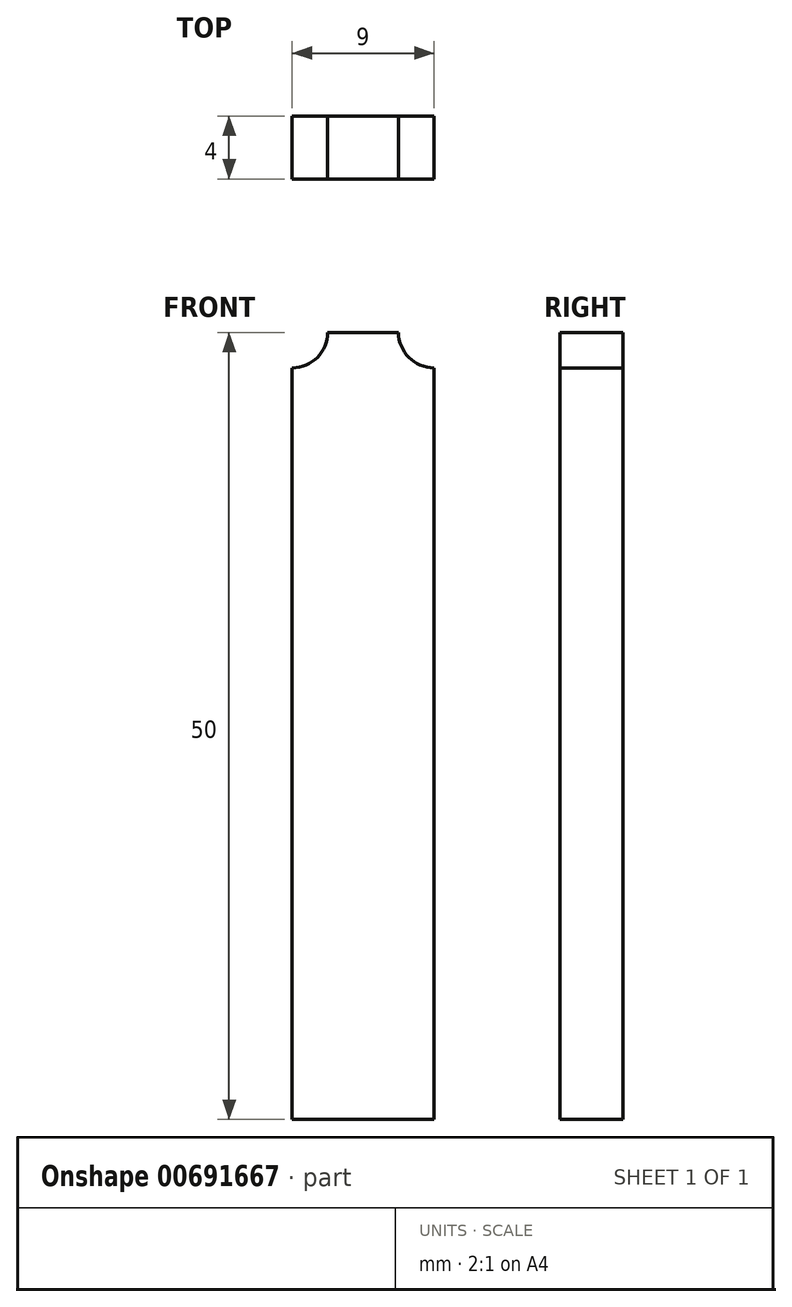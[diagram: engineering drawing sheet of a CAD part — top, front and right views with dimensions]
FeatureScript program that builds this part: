
annotation { "Feature Type Name" : "Feature", "Feature Type Description" : "" }
export const myFeature = defineFeature(function(context is Context, id is Id, definition is map)
    precondition{}
    {
        {
            var Q0;
            Q0=qCreatedBy(makeId("Front.planeOp"),FACE);
            var sketch = newSketch(context, id + "F0", { "sketchPlane" : qUnion([Q0])});
            skLineSegment(sketch, "E0.bottom", {"start": v(-4.5, 0) * mm, "end": v(4.5, 0) * mm});
            skLineSegment(sketch, "E0.top", {"start": v(-4.5, -50) * mm, "end": v(4.5, -50) * mm});
            skLineSegment(sketch, "E0.left", {"start": v(-4.5, 0) * mm, "end": v(-4.5, -50) * mm});
            skLineSegment(sketch, "E0.right", {"start": v(4.5, 0) * mm, "end": v(4.5, -50) * mm});
            skLineSegment(sketch, "E1.bottom", {"start": v(-2.25, 29.05) * mm, "end": v(2.25, 29.05) * mm});
            skLineSegment(sketch, "E1.top", {"start": v(-2.25, 0) * mm, "end": v(2.25, 0) * mm});
            skLineSegment(sketch, "E1.left", {"start": v(-2.25, 29.05) * mm, "end": v(-2.25, 0) * mm});
            skLineSegment(sketch, "E1.right", {"start": v(2.25, 29.05) * mm, "end": v(2.25, 0) * mm});
            skLineSegment(sketch, "E2", {"start": v(0, 22) * mm, "end": v(0, 13) * mm});
            skLineSegment(sketch, "E3.bottom", {"start": v(33.74, -3.72) * mm, "end": v(46.18, -3.72) * mm});
            skLineSegment(sketch, "E3.top", {"start": v(33.74, -42.5) * mm, "end": v(46.18, -42.5) * mm});
            skLineSegment(sketch, "E3.left", {"start": v(33.74, -3.72) * mm, "end": v(33.74, -42.5) * mm});
            skLineSegment(sketch, "E3.right", {"start": v(46.18, -3.72) * mm, "end": v(46.18, -42.5) * mm});
            skLineSegment(sketch, "E4", {"start": v(46.18, -8.55) * mm, "end": v(42.11, -6.2) * mm});
            skLineSegment(sketch, "E5", {"start": v(42.11, -6.2) * mm, "end": v(42.11, -13.68) * mm});
            skLineSegment(sketch, "E6", {"start": v(42.11, -13.68) * mm, "end": v(46.18, -11.33) * mm});
            skLineSegment(sketch, "E7.0.1.0", {"start": v(46.18, -20.55) * mm, "end": v(42.11, -18.2) * mm});
            skLineSegment(sketch, "E7.0.1.1", {"start": v(42.11, -18.2) * mm, "end": v(42.11, -25.68) * mm});
            skLineSegment(sketch, "E7.0.1.2", {"start": v(42.11, -25.68) * mm, "end": v(46.18, -23.33) * mm});
            skLineSegment(sketch, "E7.0.2.0", {"start": v(46.18, -32.55) * mm, "end": v(42.11, -30.2) * mm});
            skLineSegment(sketch, "E7.0.2.1", {"start": v(42.11, -30.2) * mm, "end": v(42.11, -37.68) * mm});
            skLineSegment(sketch, "E7.0.2.2", {"start": v(42.11, -37.68) * mm, "end": v(46.18, -35.33) * mm});
            skLineSegment(sketch, "E7.direction1", {"start": v(42.11, -13.68) * mm, "end": v(67.11, -13.68) * mm, "construction": true});
            skLineSegment(sketch, "E7.direction2", {"start": v(42.11, -13.68) * mm, "end": v(42.11, -25.68) * mm, "construction": true});
            skLineSegment(sketch, "E8.0", {"start": v(41.91, -14.03) * mm, "end": v(46.18, -11.57) * mm});
            skLineSegment(sketch, "E8.1", {"start": v(41.91, -5.86) * mm, "end": v(41.91, -14.03) * mm});
            skLineSegment(sketch, "E8.2", {"start": v(46.18, -8.32) * mm, "end": v(41.91, -5.86) * mm});
            skArc(sketch, "E9.0.startCap", {"start": v(-1, 22) * mm, "mid": v(0, 23) * mm, "end": v(1, 22) * mm});
            skArc(sketch, "E9.0.endCap", {"start": v(1, 13) * mm, "mid": v(0, 12) * mm, "end": v(-1, 13) * mm});
            skLineSegment(sketch, "E9.0.left", {"start": v(1, 22) * mm, "end": v(1, 13) * mm});
            skLineSegment(sketch, "E9.0.right", {"start": v(-1, 22) * mm, "end": v(-1, 13) * mm});
            skFitSpline(sketch, "E10", {"points": [v(0, 29.05) * mm, v(-1.01, 28.43) * mm, v(-1.8, 25.53) * mm, v(-2.25, 21.02) * mm], "startDerivative": vector(-5.04, -1.79) * mm, "endDerivative": vector(-0.93, -10.66) * mm});
            skFitSpline(sketch, "E11.MirrorCS", {"points": [v(0, 29.05) * mm, v(1.01, 28.43) * mm, v(1.8, 25.53) * mm, v(2.25, 21.02) * mm], "startDerivative": vector(5.04, -1.79) * mm, "endDerivative": vector(0.93, -10.66) * mm});
            skSolve(sketch);
        }
        {
            var Q0;
            {var subQ1=sQuery(id+"F0.wireOp",EDGE,"E1.top");Q0=makeQuery(id+"F0.imprint","IMPRINT",FACE,{"disambiguationData":[TD([[makeQuery(id+"F0.imprint","IMPRINT",EDGE,{"derivedFrom":subQ1}),1.0]])]});}
            var Q1;
            Q1=makeQuery(id+"F0.imprint","IMPRINT",FACE,{"disambiguationData":[TD([[makeQuery(id+"F0.imprint","IMPRINT",EDGE,{"derivedFrom":sQuery(id+"F0.wireOp",EDGE,"E0.top")}),1.0]])]});
            extrude(context, id + "F1", {"entities" : qUnion([Q0, Q1]), "depth" : 4 * mm, "offsetDistance" : 25 * mm});
        }
        {
            var Q0;
            Q0=makeQuery(id+"F1.opExtrude","CAP_FACE",FACE,{"disambiguationData":[OSD([sQuery(id+"F0.wireOp",EDGE,"E0.bottom"),sQuery(id+"F0.wireOp",EDGE,"E0.top"),sQuery(id+"F0.wireOp",EDGE,"E0.left"),sQuery(id+"F0.wireOp",EDGE,"E0.right"),sQuery(id+"F0.wireOp",EDGE,"E1.left"),sQuery(id+"F0.wireOp",EDGE,"E1.right"),sQuery(id+"F0.wireOp",EDGE,"E9.0.startCap"),sQuery(id+"F0.wireOp",EDGE,"E9.0.endCap"),sQuery(id+"F0.wireOp",EDGE,"E9.0.left"),sQuery(id+"F0.wireOp",EDGE,"E9.0.right"),sQuery(id+"F0.wireOp",EDGE,"E10"),sQuery(id+"F0.wireOp",EDGE,"E11.MirrorCS")])],"isStart":false});
            var sketch = newSketch(context, id + "F2", { "sketchPlane" : qUnion([Q0])});
            skCircle(sketch, "E12", {"center": v(4.5, 0) * mm, "radius": 2.25 * mm});
            skCircle(sketch, "E13", {"center": v(-4.5, 0) * mm, "radius": 2.25 * mm});
            skSolve(sketch);
        }
        {
            var Q0;
            {var subQ2=sQuery(id+"F0.wireOp",EDGE,"E0.right");var subQ3=sQuery(id+"F0.wireOp",EDGE,"E0.bottom");var subQ4=makeQuery(id+"F1.opExtrude","CAP_EDGE",EDGE,{"disambiguationData":[OSD([subQ3]),TDD([makeQuery(id+"F0.imprint","IMPRINT",EDGE,{"disambiguationData":[TD([[makeQuery(id+"F0.imprint","INTERSECT",VERTEX,{"derivedFrom":[subQ3,subQ2]}),1.0]])],"derivedFrom":subQ3})])],"isStart":false});Q0=makeQuery(id+"F2.imprint","IMPRINT",FACE,{"disambiguationData":[TD([[makeQuery(id+"F2.imprint","IMPRINT",EDGE,{"derivedFrom":subQ4}),-1.0]])]});}
            var Q1;
            {var subQ2=sQuery(id+"F0.wireOp",EDGE,"E0.left");var subQ3=sQuery(id+"F0.wireOp",EDGE,"E0.bottom");var subQ4=makeQuery(id+"F1.opExtrude","CAP_EDGE",EDGE,{"disambiguationData":[OSD([subQ3]),TDD([makeQuery(id+"F0.imprint","IMPRINT",EDGE,{"disambiguationData":[TD([[makeQuery(id+"F0.imprint","INTERSECT",VERTEX,{"derivedFrom":[subQ3,subQ2]}),-1.0]])],"derivedFrom":subQ3})])],"isStart":false});Q1=makeQuery(id+"F2.imprint","IMPRINT",FACE,{"disambiguationData":[TD([[makeQuery(id+"F2.imprint","IMPRINT",EDGE,{"derivedFrom":subQ4}),-1.0]])]});}
            extrude(context, id + "F3", {"entities" : qUnion([Q0, Q1]), "operationType" : NewBodyOperationType.REMOVE, "endBound" : BoundingType.THROUGH_ALL, "oppositeDirection" : true, "depth" : 25 * mm, "offsetDistance" : 25 * mm});
        }
        {
            var Q0;
            Q0=qCreatedBy(makeId("Right.planeOp"),FACE);
            var sketch = newSketch(context, id + "F4", { "sketchPlane" : qUnion([Q0])});
            skLineSegment(sketch, "E14", {"start": v(0, 29.15) * mm, "end": v(-1.6, 29.15) * mm});
            skLineSegment(sketch, "E15", {"start": v(-1.6, 29.15) * mm, "end": v(0, 21.06) * mm});
            skLineSegment(sketch, "E16", {"start": v(0, 21.06) * mm, "end": v(0, 29.15) * mm});
            skLineSegment(sketch, "E17", {"start": v(-2.4, 29.15) * mm, "end": v(-4, 29.15) * mm});
            skLineSegment(sketch, "E18", {"start": v(-4, 29.15) * mm, "end": v(-4, 21.06) * mm});
            skLineSegment(sketch, "E19", {"start": v(-4, 21.06) * mm, "end": v(-2.4, 29.15) * mm});
            skSolve(sketch);
        }
        {
            var Q0;
            Q0=makeQuery(id+"F4.imprint","IMPRINT",FACE,{"disambiguationData":[TD([[makeQuery(id+"F4.imprint","IMPRINT",EDGE,{"derivedFrom":sQuery(id+"F4.wireOp",EDGE,"E17")}),1.0]])]});
            var Q1;
            Q1=makeQuery(id+"F4.imprint","IMPRINT",FACE,{"disambiguationData":[TD([[makeQuery(id+"F4.imprint","IMPRINT",EDGE,{"derivedFrom":sQuery(id+"F4.wireOp",EDGE,"E14")}),1.0]])]});
            extrude(context, id + "F5", {"entities" : qUnion([Q0, Q1]), "operationType" : NewBodyOperationType.REMOVE, "endBound" : BoundingType.SYMMETRIC, "oppositeDirection" : true, "depth" : 25 * mm, "offsetDistance" : 25 * mm});
        }
    });
